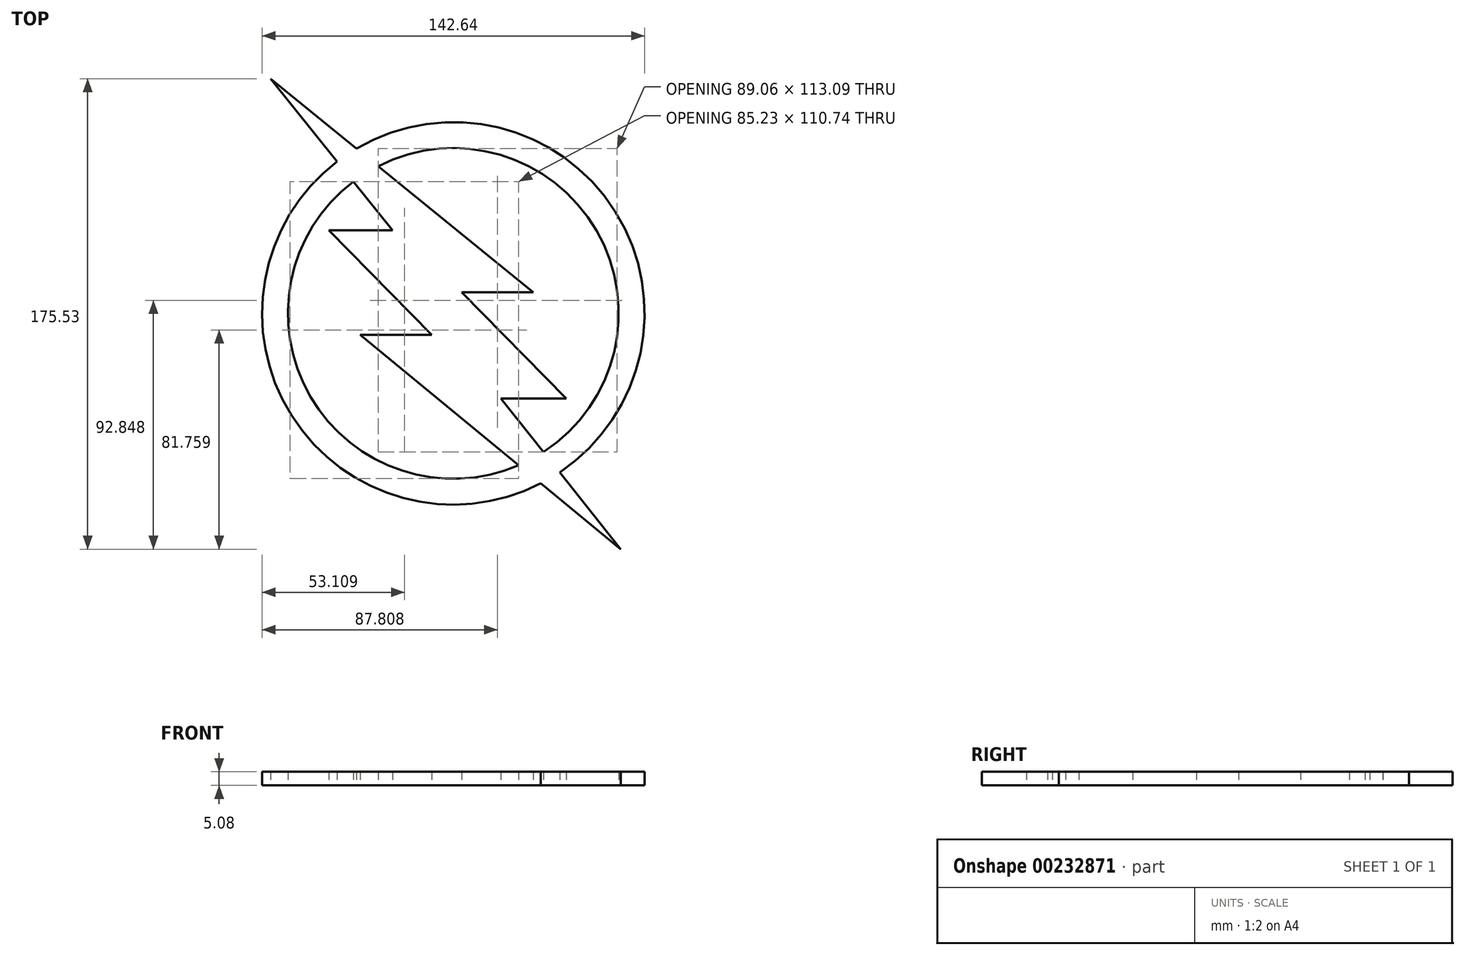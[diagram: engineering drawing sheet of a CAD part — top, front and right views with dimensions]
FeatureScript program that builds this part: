
annotation { "Feature Type Name" : "Feature", "Feature Type Description" : "" }
export const myFeature = defineFeature(function(context is Context, id is Id, definition is map)
    precondition{}
    {
        {
            var Q0;
            Q0=qCreatedBy(makeId("Top.planeOp"),FACE);
            var sketch = newSketch(context, id + "F0", { "sketchPlane" : qUnion([Q0])});
            skLineSegment(sketch, "E0", {"start": v(-62.73, 79.67) * mm, "end": v(35.14, 0) * mm});
            skLineSegment(sketch, "E1", {"start": v(35.14, 0) * mm, "end": v(8.57, 0) * mm});
            skLineSegment(sketch, "E2", {"start": v(8.57, 0) * mm, "end": v(47.52, -39.57) * mm});
            skLineSegment(sketch, "E3", {"start": v(47.52, -39.57) * mm, "end": v(23.1, -39.57) * mm});
            skLineSegment(sketch, "E4", {"start": v(23.1, -39.57) * mm, "end": v(67.89, -95.86) * mm});
            skLineSegment(sketch, "E5", {"start": v(67.89, -95.86) * mm, "end": v(-29.34, -15.83) * mm});
            skLineSegment(sketch, "E6", {"start": v(-29.34, -15.83) * mm, "end": v(-2.66, -15.83) * mm});
            skLineSegment(sketch, "E7", {"start": v(-2.66, -15.83) * mm, "end": v(-41, 23.1) * mm});
            skLineSegment(sketch, "E8", {"start": v(-41, 23.1) * mm, "end": v(-17.29, 23.1) * mm});
            skLineSegment(sketch, "E9", {"start": v(-17.29, 23.1) * mm, "end": v(-62.73, 79.67) * mm});
            skArc(sketch, "E10", {"start": v(45.03, -67.14) * mm, "mid": v(65.79, 30.04) * mm, "end": v(-30.74, 53.63) * mm});
            skArc(sketch, "E11.0", {"start": v(39, -59.56) * mm, "mid": v(58.76, 23) * mm, "end": v(-22.66, 47.05) * mm});
            skArc(sketch, "E12.trimOffspring", {"start": v(-31.88, 41.27) * mm, "mid": v(-47.9, -38.93) * mm, "end": v(29.78, -64.5) * mm});
            skArc(sketch, "E13.trimOffspring", {"start": v(-37.93, 48.8) * mm, "mid": v(-54.9, -45.99) * mm, "end": v(38.02, -71.28) * mm});
            skSolve(sketch);
        }
        {
            var Q0;
            {var subQ19=sQuery(id+"F0.wireOp",EDGE,"E1");Q0=makeQuery(id+"F0.imprint","IMPRINT",FACE,{"disambiguationData":[TD([[makeQuery(id+"F0.imprint","IMPRINT",EDGE,{"derivedFrom":subQ19}),-1.0]])]});}
            var Q1;
            {var subQ0=sQuery(id+"F0.wireOp",EDGE,"E12.trimOffspring");Q1=makeQuery(id+"F0.imprint","IMPRINT",FACE,{"disambiguationData":[TD([[makeQuery(id+"F0.imprint","IMPRINT",EDGE,{"derivedFrom":subQ0}),-1.0]])]});}
            var Q2;
            {var subQ0=sQuery(id+"F0.wireOp",EDGE,"E10");Q2=makeQuery(id+"F0.imprint","IMPRINT",FACE,{"disambiguationData":[TD([[makeQuery(id+"F0.imprint","IMPRINT",EDGE,{"derivedFrom":subQ0}),1.0]])]});}
            extrude(context, id + "F1", {"entities" : qUnion([Q0, Q1, Q2]), "depth" : 5.08 * mm});
        }
    });
